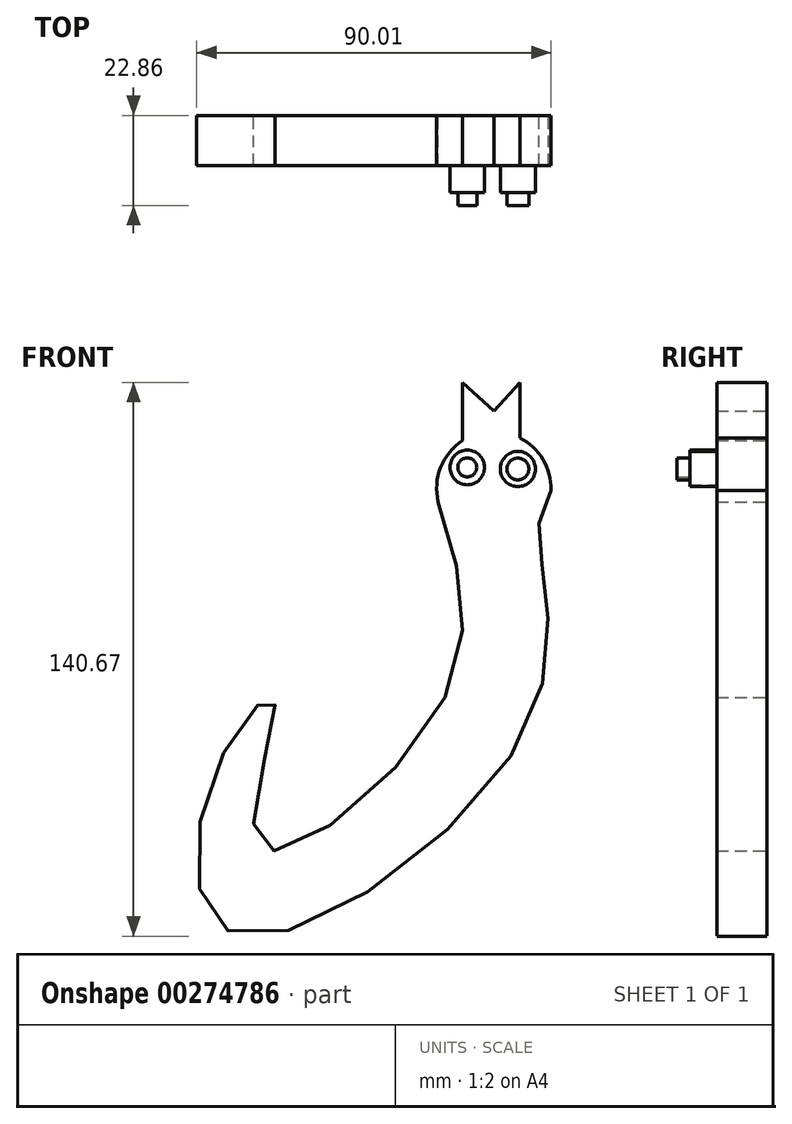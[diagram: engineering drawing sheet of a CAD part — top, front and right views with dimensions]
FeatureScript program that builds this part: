
annotation { "Feature Type Name" : "Feature", "Feature Type Description" : "" }
export const myFeature = defineFeature(function(context is Context, id is Id, definition is map)
    precondition{}
    {
        {
            var Q0;
            Q0=qCreatedBy(makeId("Front.planeOp"),FACE);
            var sketch = newSketch(context, id + "F0", { "sketchPlane" : qUnion([Q0])});
            skArc(sketch, "E0", {"start": v(14.51, 43.73) * mm, "mid": v(-1.5, 58.6) * mm, "end": v(-14.11, 40.75) * mm});
            skFitSpline(sketch, "E1", {"points": [v(-14.11, 40.75) * mm, v(-14.11, -12.27) * mm, v(-59.83, -46.29) * mm, v(-55.68, -9.78) * mm, v(-70.62, -27.2) * mm, v(-66.47, -68.69) * mm, v(6.55, -20.15) * mm, v(11.94, 27.56) * mm, v(14.51, 43.73) * mm], "startDerivative": vector(118.81, -378.36) * mm, "endDerivative": vector(132.46, 190.53) * mm});
            skLineSegment(sketch, "E2", {"start": v(-7.9, 56.34) * mm, "end": v(-7.9, 71.12) * mm});
            skLineSegment(sketch, "E3", {"start": v(-7.9, 71.12) * mm, "end": v(0, 63.87) * mm});
            skLineSegment(sketch, "E4", {"start": v(0, 63.87) * mm, "end": v(6.66, 71.12) * mm});
            skLineSegment(sketch, "E5", {"start": v(6.66, 71.12) * mm, "end": v(6.66, 57.05) * mm});
            skSolve(sketch);
        }
        {
            var Q0;
            {var subQ0=sQuery(id+"F0.wireOp",EDGE,"E1");Q0=makeQuery(id+"F0.imprint","IMPRINT",FACE,{"disambiguationData":[TD([[makeQuery(id+"F0.imprint","IMPRINT",EDGE,{"derivedFrom":subQ0}),1.0]])]});}
            var Q1;
            {var subQ0=sQuery(id+"F0.wireOp",EDGE,"E2");Q1=makeQuery(id+"F0.imprint","IMPRINT",FACE,{"disambiguationData":[TD([[makeQuery(id+"F0.imprint","IMPRINT",EDGE,{"derivedFrom":subQ0}),-1.0]])]});}
            extrude(context, id + "F1", {"entities" : qUnion([Q0, Q1]), "depth" : 12.7 * mm});
        }
        {
            var Q0;
            Q0=makeQuery(id+"F1.opExtrude","CAP_FACE",FACE,{"disambiguationData":[OSD([sQuery(id+"F0.wireOp",EDGE,"E0"),sQuery(id+"F0.wireOp",EDGE,"E1"),sQuery(id+"F0.wireOp",EDGE,"E2"),sQuery(id+"F0.wireOp",EDGE,"E3"),sQuery(id+"F0.wireOp",EDGE,"E4"),sQuery(id+"F0.wireOp",EDGE,"E5")])],"isStart":false});
            var sketch = newSketch(context, id + "F2", { "sketchPlane" : qUnion([Q0])});
            skCircle(sketch, "E6", {"center": v(-6.73, 49.53) * mm, "radius": 4.4 * mm});
            skPoint(sketch, "E6.centerSnap0", {"position": v(-13.49, 49.53) * mm});
            skCircle(sketch, "E7", {"center": v(6.13, 49.13) * mm, "radius": 4.47 * mm});
            skSolve(sketch);
        }
        {
            var Q0;
            Q0 = qSketchRegion(id + "F2", true);
            extrude(context, id + "F3", {"entities" : qUnion([Q0]), "operationType" : NewBodyOperationType.ADD, "depth" : 6.86 * mm});
        }
        {
            var Q0;
            Q0=makeQuery(id+"F1.opExtrude","CAP_FACE",FACE,{"disambiguationData":[OSD([sQuery(id+"F0.wireOp",EDGE,"E0"),sQuery(id+"F0.wireOp",EDGE,"E1"),sQuery(id+"F0.wireOp",EDGE,"E2"),sQuery(id+"F0.wireOp",EDGE,"E3"),sQuery(id+"F0.wireOp",EDGE,"E4"),sQuery(id+"F0.wireOp",EDGE,"E5")])],"isStart":false});
            var sketch = newSketch(context, id + "F4", { "sketchPlane" : qUnion([Q0])});
            skCircle(sketch, "E8", {"center": v(-6.73, 49.53) * mm, "radius": 2.4 * mm});
            skSolve(sketch);
        }
        {
            var Q0;
            Q0 = qSketchRegion(id + "F4", true);
            extrude(context, id + "F5", {"entities" : qUnion([Q0]), "operationType" : NewBodyOperationType.ADD, "depth" : 10.16 * mm});
        }
        {
            var Q0;
            Q0=makeQuery(id+"F3.opExtrude","CAP_FACE",FACE,{"disambiguationData":[OSD([sQuery(id+"F2.wireOp",EDGE,"E7")])],"isStart":false});
            var sketch = newSketch(context, id + "F6", { "sketchPlane" : qUnion([Q0])});
            skCircle(sketch, "E9", {"center": v(6.13, 49.13) * mm, "radius": 2.78 * mm});
            skSolve(sketch);
        }
        {
            var Q0;
            Q0 = qSketchRegion(id + "F6", true);
            extrude(context, id + "F7", {"entities" : qUnion([Q0]), "operationType" : NewBodyOperationType.ADD, "depth" : 3.3 * mm});
        }
    });
